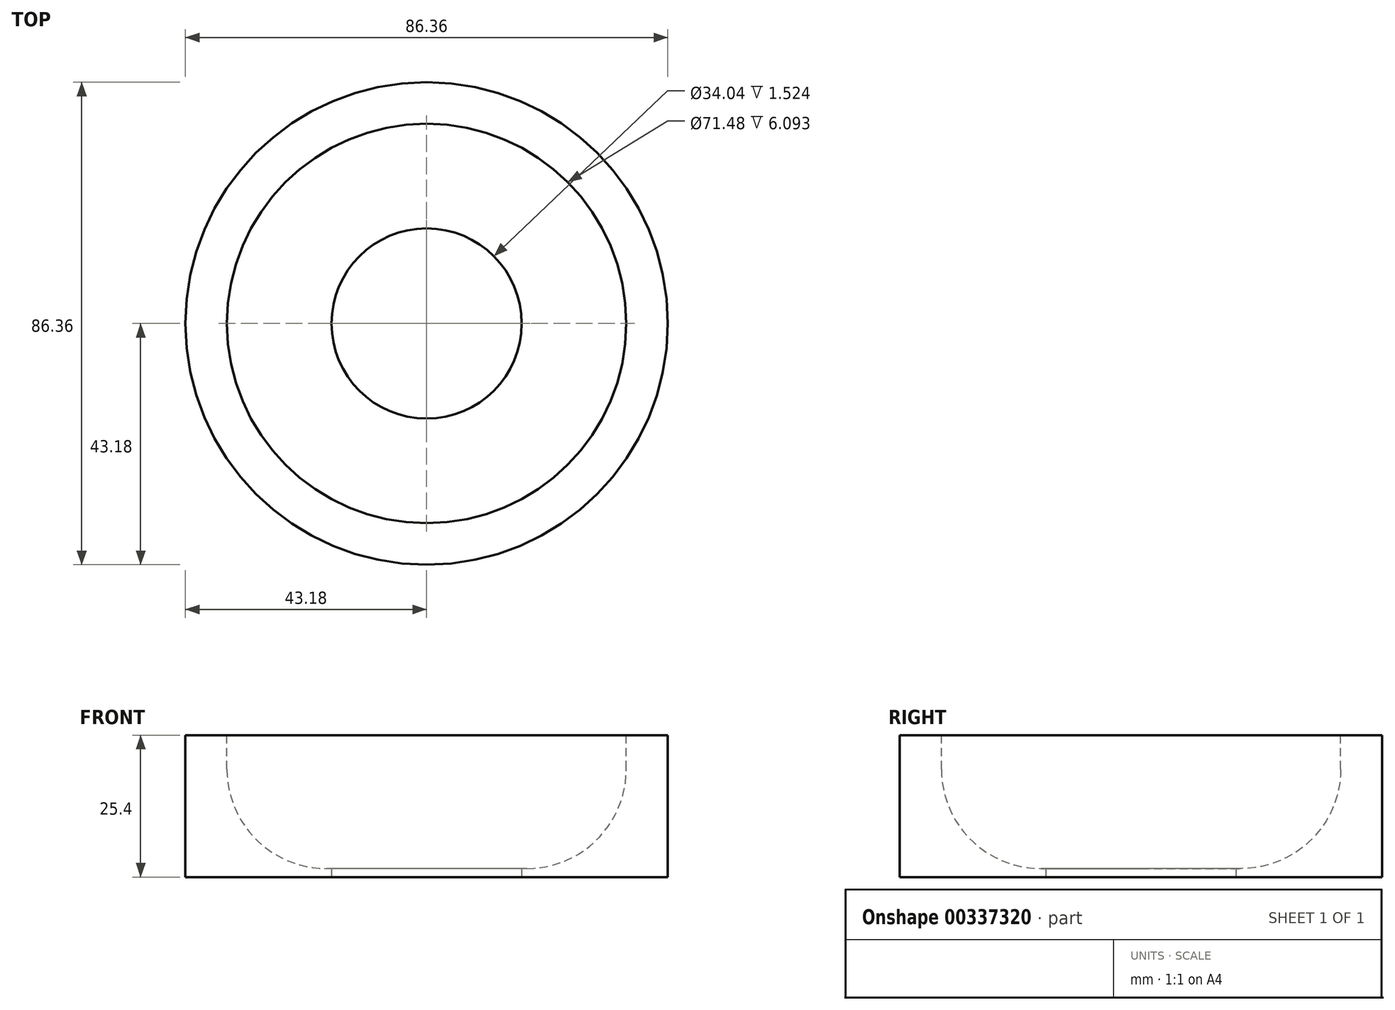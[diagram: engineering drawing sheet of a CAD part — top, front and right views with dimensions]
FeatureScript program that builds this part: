
annotation { "Feature Type Name" : "Feature", "Feature Type Description" : "" }
export const myFeature = defineFeature(function(context is Context, id is Id, definition is map)
    precondition{}
    {
        {
            var Q0;
            Q0=qCreatedBy(makeId("Top.planeOp"),FACE);
            var sketch = newSketch(context, id + "F0", { "sketchPlane" : qUnion([Q0])});
            skCircle(sketch, "E0", {"center": v(0, 0) * mm, "radius": 43.18 * mm});
            skSolve(sketch);
        }
        {
            var Q0;
            Q0=makeQuery(id+"F0.imprint","IMPRINT",FACE,{"disambiguationData":[TD([[makeQuery(id+"F0.imprint","IMPRINT",EDGE,{"derivedFrom":sQuery(id+"F0.wireOp",EDGE,"E0")}),1.0]])]});
            extrude(context, id + "F1", {"entities" : qUnion([Q0]), "depth" : 25.4 * mm});
        }
        {
            var Q0;
            Q0=makeQuery(id+"F0.imprint","IMPRINT",FACE,{"disambiguationData":[TD([[makeQuery(id+"F0.imprint","IMPRINT",EDGE,{"derivedFrom":sQuery(id+"F0.wireOp",EDGE,"E0")}),1.0]])]});
            var sketch = newSketch(context, id + "F2", { "sketchPlane" : qUnion([Q0])});
            skCircle(sketch, "E1", {"center": v(0, 0) * mm, "radius": 17.02 * mm});
            skSolve(sketch);
        }
        {
            var Q0;
            Q0 = qSketchRegion(id + "F2", true);
            extrude(context, id + "F3", {"entities" : qUnion([Q0]), "operationType" : NewBodyOperationType.REMOVE, "depth" : 27.7 * mm});
        }
        {
            var Q0;
            Q0=makeQuery(id+"F1.opExtrude","CAP_FACE",FACE,{"disambiguationData":[OSD([sQuery(id+"F0.wireOp",EDGE,"E0")])],"isStart":false});
            var sketch = newSketch(context, id + "F4", { "sketchPlane" : qUnion([Q0])});
            skCircle(sketch, "E2", {"center": v(0, 0) * mm, "radius": 35.74 * mm});
            skSolve(sketch);
        }
        {
            var Q0;
            Q0 = qSketchRegion(id + "F4", true);
            extrude(context, id + "F5", {"entities" : qUnion([Q0]), "operationType" : NewBodyOperationType.REMOVE, "oppositeDirection" : true, "depth" : 23.88 * mm});
        }
        {
            var Q0;
            Q0=makeQuery(id+"F5.boolean.opBoolean","COPY",EDGE,{"derivedFrom":makeQuery(id+"F5.opExtrude","CAP_EDGE",EDGE,{"disambiguationData":[OSD([sQuery(id+"F4.wireOp",EDGE,"E2")])],"isStart":false})});
            fillet(context, id + "F6", {"entities" : qUnion([Q0]), "radius" : 17.78 * mm, "allowEdgeOverflow" : false});
        }
    });
